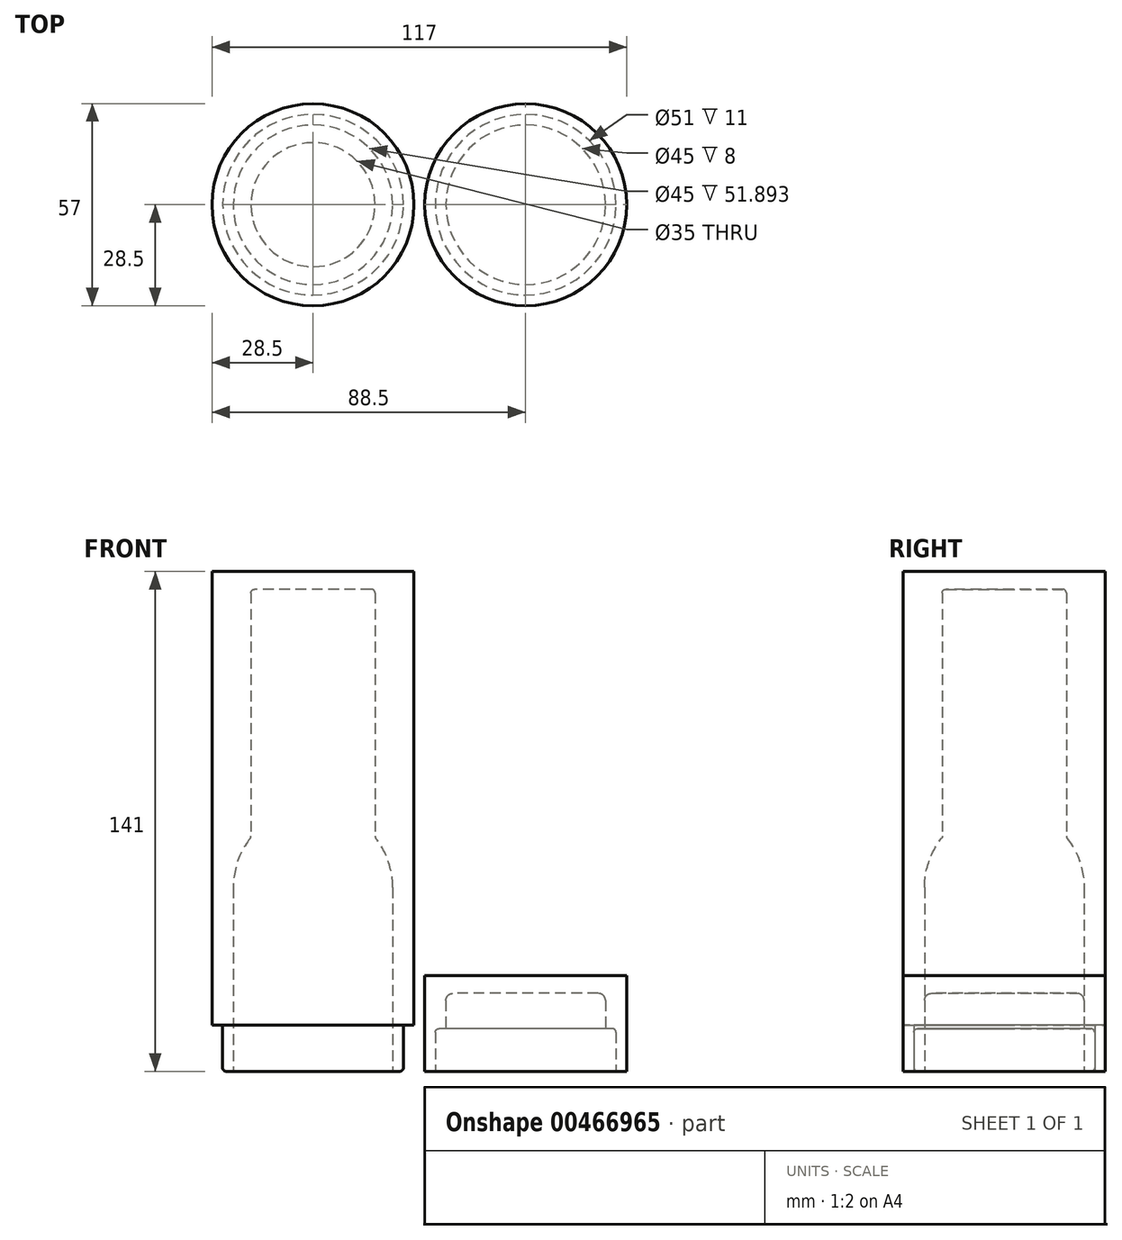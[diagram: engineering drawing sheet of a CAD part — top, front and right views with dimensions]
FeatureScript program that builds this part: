
annotation { "Feature Type Name" : "Feature", "Feature Type Description" : "" }
export const myFeature = defineFeature(function(context is Context, id is Id, definition is map)
    precondition{}
    {
        {
            var Q0;
            Q0=qCreatedBy(makeId("Top.planeOp"),FACE);
            var sketch = newSketch(context, id + "F0", { "sketchPlane" : qUnion([Q0])});
            skCircle(sketch, "E0", {"center": v(0, 0) * mm, "radius": 22.5 * mm});
            skCircle(sketch, "E1", {"center": v(0, 0) * mm, "radius": 17.5 * mm});
            skCircle(sketch, "E2", {"center": v(0, 0) * mm, "radius": 25.5 * mm});
            skSolve(sketch);
        }
        {
            var Q0;
            Q0 = qSketchRegion(id + "F0", true);
            var Q1;
            Q1=makeQuery(id+"F0.imprint","IMPRINT",FACE,{"disambiguationData":[TD([[makeQuery(id+"F0.imprint","IMPRINT",EDGE,{"derivedFrom":sQuery(id+"F0.wireOp",EDGE,"E0")}),1.0]])]});
            var Q2;
            Q2=makeQuery(id+"F0.imprint","IMPRINT",FACE,{"disambiguationData":[TD([[makeQuery(id+"F0.imprint","IMPRINT",EDGE,{"derivedFrom":sQuery(id+"F0.wireOp",EDGE,"E1")}),1.0]])]});
            extrude(context, id + "F1", {"entities" : qUnion([Q0, Q1, Q2]), "depth" : 141 * mm});
        }
        {
            var Q0;
            Q0=makeQuery(id+"F0.imprint","IMPRINT",FACE,{"disambiguationData":[TD([[makeQuery(id+"F0.imprint","IMPRINT",EDGE,{"derivedFrom":sQuery(id+"F0.wireOp",EDGE,"E1")}),1.0]])]});
            extrude(context, id + "F2", {"entities" : qUnion([Q0]), "operationType" : NewBodyOperationType.REMOVE, "depth" : 136 * mm});
        }
        {
            var Q0;
            Q0=makeQuery(id+"F0.imprint","IMPRINT",FACE,{"disambiguationData":[TD([[makeQuery(id+"F0.imprint","IMPRINT",EDGE,{"derivedFrom":sQuery(id+"F0.wireOp",EDGE,"E0")}),1.0]])]});
            extrude(context, id + "F3", {"entities" : qUnion([Q0]), "operationType" : NewBodyOperationType.REMOVE, "depth" : 66 * mm});
        }
        {
            var Q0;
            Q0=makeQuery(id+"F3.boolean.opBoolean","COPY",EDGE,{"derivedFrom":makeQuery(id+"F3.opExtrude","CAP_EDGE",EDGE,{"disambiguationData":[OSD([sQuery(id+"F0.wireOp",EDGE,"E0")])],"isStart":false})});
            fillet(context, id + "F4", {"entities" : qUnion([Q0]), "radius" : 22.4 * mm, "tangentPropagation" : true, "allowEdgeOverflow" : false});
        }
        {
            var Q0;
            Q0=makeQuery(id+"F2.boolean.opBoolean","COPY",EDGE,{"derivedFrom":makeQuery(id+"F2.opExtrude","CAP_EDGE",EDGE,{"disambiguationData":[OSD([sQuery(id+"F0.wireOp",EDGE,"E1")])],"isStart":false})});
            fillet(context, id + "F5", {"entities" : qUnion([Q0]), "radius" : 1 * mm, "tangentPropagation" : true, "allowEdgeOverflow" : false});
        }
        {
            var Q0;
            Q0=makeQuery(id+"F4.opFillet","BLEND_EDGE",EDGE,{"blendedFrom":[makeQuery(id+"F3.boolean.opBoolean","COPY",EDGE,{"derivedFrom":makeQuery(id+"F3.opExtrude","CAP_EDGE",EDGE,{"disambiguationData":[OSD([sQuery(id+"F0.wireOp",EDGE,"E0")])],"isStart":false})}),makeQuery(id+"F2.boolean.opBoolean","COPY",FACE,{"derivedFrom":makeQuery(id+"F2.opExtrude","SWEPT_FACE",FACE,{"disambiguationData":[OSD([sQuery(id+"F0.wireOp",EDGE,"E1")])]})})],"blendedInto":[makeQuery(id+"F2.boolean.opBoolean","COPY",FACE,{"derivedFrom":makeQuery(id+"F2.opExtrude","SWEPT_FACE",FACE,{"disambiguationData":[OSD([sQuery(id+"F0.wireOp",EDGE,"E1")])]})})]});
            fillet(context, id + "F6", {"entities" : qUnion([Q0]), "radius" : 1 * mm, "tangentPropagation" : true, "allowEdgeOverflow" : false});
        }
        {
            var Q0;
            Q0=makeQuery(id+"F1.opExtrude","CAP_EDGE",EDGE,{"disambiguationData":[OSD([sQuery(id+"F0.wireOp",EDGE,"E2")])],"isStart":true});
            fillet(context, id + "F7", {"entities" : qUnion([Q0]), "radius" : 1 * mm, "tangentPropagation" : true, "allowEdgeOverflow" : false});
        }
        {
            var Q0;
            Q0=qCreatedBy(makeId("Top.planeOp"),FACE);
            var sketch = newSketch(context, id + "F8", { "sketchPlane" : qUnion([Q0])});
            skLineSegment(sketch, "E3", {"start": v(0, 0) * mm, "end": v(60, 0) * mm, "construction": true});
            skCircle(sketch, "E4", {"center": v(60, 0) * mm, "radius": 25.5 * mm});
            skCircle(sketch, "E5", {"center": v(60, 0) * mm, "radius": 28.5 * mm});
            skCircle(sketch, "E6", {"center": v(60, 0) * mm, "radius": 22.5 * mm});
            skSolve(sketch);
        }
        {
            var Q0;
            Q0 = qSketchRegion(id + "F8", true);
            var Q1;
            Q1=makeQuery(id+"F8.imprint","IMPRINT",FACE,{"disambiguationData":[TD([[makeQuery(id+"F8.imprint","IMPRINT",EDGE,{"derivedFrom":sQuery(id+"F8.wireOp",EDGE,"E6")}),1.0]])]});
            var Q2;
            Q2=makeQuery(id+"F8.imprint","IMPRINT",FACE,{"disambiguationData":[TD([[makeQuery(id+"F8.imprint","IMPRINT",EDGE,{"derivedFrom":sQuery(id+"F8.wireOp",EDGE,"E4")}),1.0]])]});
            extrude(context, id + "F9", {"entities" : qUnion([Q0, Q1, Q2]), "depth" : 27 * mm});
        }
        {
            var Q0;
            Q0=makeQuery(id+"F8.imprint","IMPRINT",FACE,{"disambiguationData":[TD([[makeQuery(id+"F8.imprint","IMPRINT",EDGE,{"derivedFrom":sQuery(id+"F8.wireOp",EDGE,"E6")}),1.0]])]});
            extrude(context, id + "F10", {"entities" : qUnion([Q0]), "operationType" : NewBodyOperationType.REMOVE, "depth" : 22 * mm});
        }
        {
            var Q0;
            Q0=makeQuery(id+"F8.imprint","IMPRINT",FACE,{"disambiguationData":[TD([[makeQuery(id+"F8.imprint","IMPRINT",EDGE,{"derivedFrom":sQuery(id+"F8.wireOp",EDGE,"E4")}),1.0]])]});
            extrude(context, id + "F11", {"entities" : qUnion([Q0]), "operationType" : NewBodyOperationType.REMOVE, "depth" : 12 * mm});
        }
        {
            var Q0;
            Q0=makeQuery(id+"F10.boolean.opBoolean","COPY",EDGE,{"derivedFrom":makeQuery(id+"F10.opExtrude","CAP_EDGE",EDGE,{"disambiguationData":[OSD([sQuery(id+"F8.wireOp",EDGE,"E6")])],"isStart":false})});
            fillet(context, id + "F12", {"entities" : qUnion([Q0]), "radius" : 2 * mm, "tangentPropagation" : true, "allowEdgeOverflow" : false});
        }
        {
            var Q0;
            Q0=makeQuery(id+"F11.boolean.opBoolean","COPY",EDGE,{"derivedFrom":makeQuery(id+"F11.opExtrude","CAP_EDGE",EDGE,{"disambiguationData":[OSD([sQuery(id+"F8.wireOp",EDGE,"E4")])],"isStart":false})});
            fillet(context, id + "F13", {"entities" : qUnion([Q0]), "radius" : 1 * mm, "tangentPropagation" : true, "allowEdgeOverflow" : false});
        }
        {
            var Q0;
            Q0=makeQuery(id+"F1.opExtrude","CAP_FACE",FACE,{"disambiguationData":[OSD([sQuery(id+"F0.wireOp",EDGE,"E2")])],"isStart":false});
            var sketch = newSketch(context, id + "F14", { "sketchPlane" : qUnion([Q0])});
            skCircle(sketch, "E7", {"center": v(0, 0) * mm, "radius": 28.5 * mm});
            skSolve(sketch);
        }
        {
            var Q0;
            Q0=makeQuery(id+"F14.imprint","IMPRINT",FACE,{"disambiguationData":[TD([[makeQuery(id+"F14.imprint","IMPRINT",EDGE,{"derivedFrom":sQuery(id+"F14.wireOp",EDGE,"E7")}),1.0]])]});
            extrude(context, id + "F15", {"entities" : qUnion([Q0]), "operationType" : NewBodyOperationType.ADD, "oppositeDirection" : true, "depth" : 128 * mm});
        }
    });
